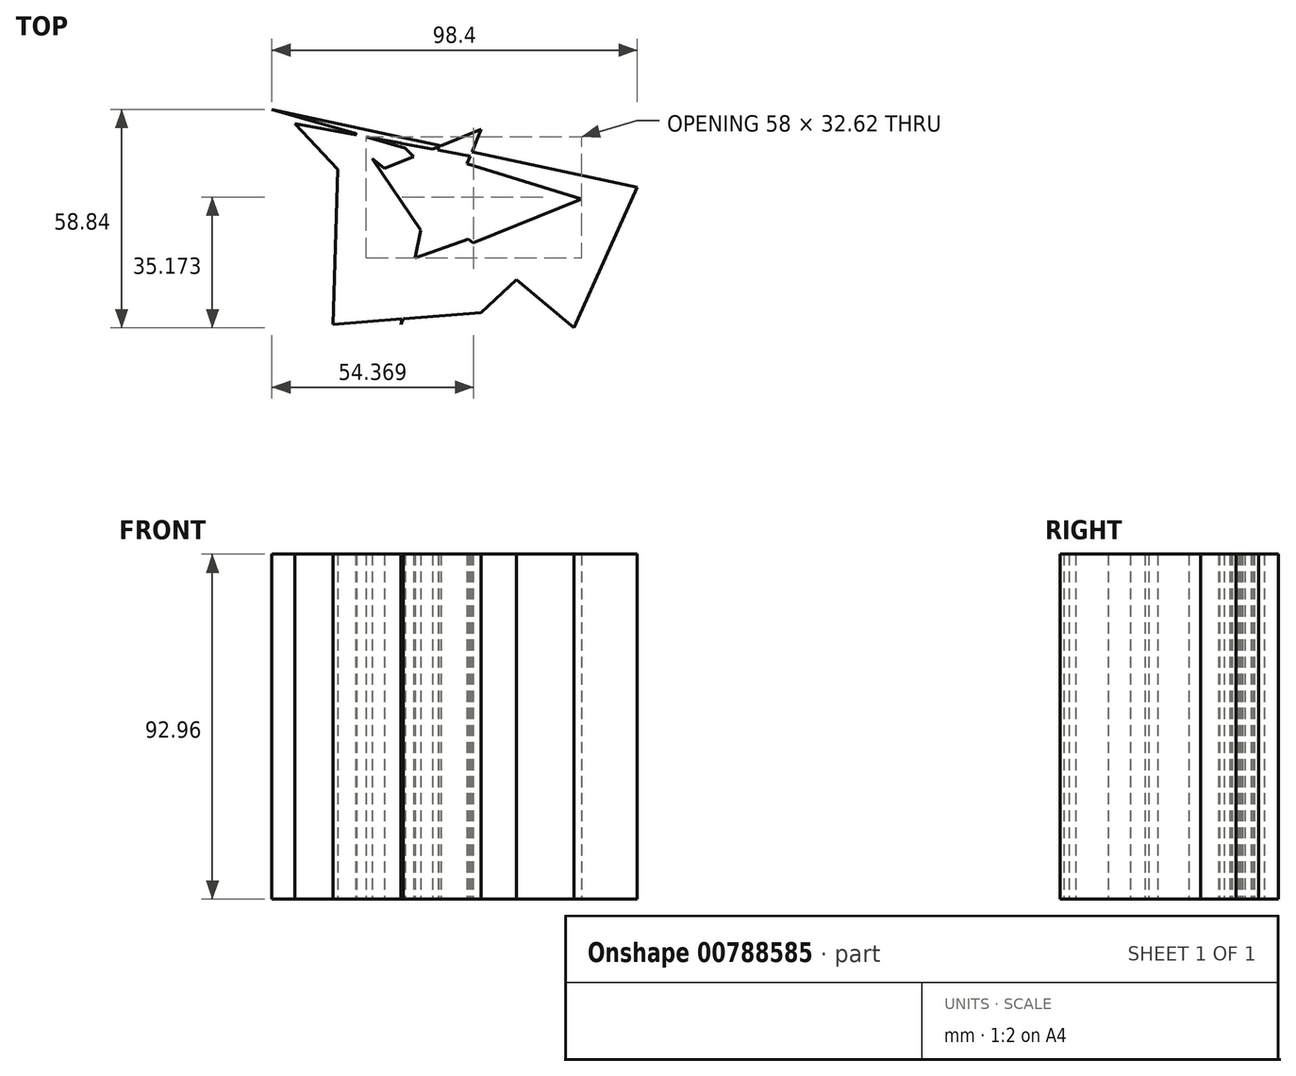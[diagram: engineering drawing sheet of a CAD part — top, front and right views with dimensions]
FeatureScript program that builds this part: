
annotation { "Feature Type Name" : "Feature", "Feature Type Description" : "" }
export const myFeature = defineFeature(function(context is Context, id is Id, definition is map)
    precondition{}
    {
        {
            var Q0;
            Q0=qCreatedBy(makeId("Top.planeOp"),FACE);
            var sketch = newSketch(context, id + "F0", { "sketchPlane" : qUnion([Q0])});
            skLineSegment(sketch, "E0", {"start": v(-35.04, 43.44) * mm, "end": v(24.92, -20.53) * mm});
            skLineSegment(sketch, "E1", {"start": v(-7.92, 44.78) * mm, "end": v(-21.67, -19.57) * mm});
            skLineSegment(sketch, "E2", {"start": v(-21.67, -19.57) * mm, "end": v(0, 32.94) * mm});
            skLineSegment(sketch, "E3", {"start": v(0, 32.94) * mm, "end": v(-38.63, 17.28) * mm});
            skLineSegment(sketch, "E4", {"start": v(-25.41, 44.78) * mm, "end": v(-18.19, 78.6) * mm});
            skLineSegment(sketch, "E5", {"start": v(-46.23, -11.67) * mm, "end": v(0, 4.63) * mm});
            skLineSegment(sketch, "E6", {"start": v(11.23, 38.89) * mm, "end": v(-23.94, 51.66) * mm});
            skLineSegment(sketch, "E7", {"start": v(-53.73, 61.35) * mm, "end": v(-16.27, 5.71) * mm});
            skLineSegment(sketch, "E8", {"start": v(-7.92, 0) * mm, "end": v(26.96, 14.14) * mm});
            skLineSegment(sketch, "E9", {"start": v(26.96, 14.14) * mm, "end": v(-38.63, 34.5) * mm});
            skLineSegment(sketch, "E10", {"start": v(-38.63, 34.5) * mm, "end": v(42, 17.28) * mm});
            skLineSegment(sketch, "E11", {"start": v(42, 17.28) * mm, "end": v(-56.41, 38.3) * mm});
            skLineSegment(sketch, "E12", {"start": v(-56.41, 38.3) * mm, "end": v(26.96, 14.14) * mm});
            skLineSegment(sketch, "E13", {"start": v(31.14, 12.78) * mm, "end": v(0, -16.4) * mm});
            skLineSegment(sketch, "E14", {"start": v(0, -16.4) * mm, "end": v(-39.95, -19.57) * mm});
            skLineSegment(sketch, "E15", {"start": v(-39.95, -19.57) * mm, "end": v(-38.63, 22.1) * mm});
            skLineSegment(sketch, "E16", {"start": v(-38.63, 22.1) * mm, "end": v(-50.27, 34.5) * mm});
            skLineSegment(sketch, "E17", {"start": v(-50.27, 34.5) * mm, "end": v(36.36, 18.49) * mm});
            skLineSegment(sketch, "E18", {"start": v(36.36, 18.49) * mm, "end": v(31.14, 12.78) * mm});
            skLineSegment(sketch, "E19", {"start": v(-18.19, 78.6) * mm, "end": v(42, 17.28) * mm});
            skLineSegment(sketch, "E20", {"start": v(42, 17.28) * mm, "end": v(24.92, -20.53) * mm});
            skLineSegment(sketch, "E21", {"start": v(24.92, -20.53) * mm, "end": v(-38.63, 32.94) * mm});
            skSolve(sketch);
        }
        {
            var Q0;
            Q0 = qSketchRegion(id + "F0", true);
            extrude(context, id + "F1", {"entities" : qUnion([Q0]), "depth" : 92.96 * mm, "offsetDistance" : 25.4 * mm});
        }
    });
